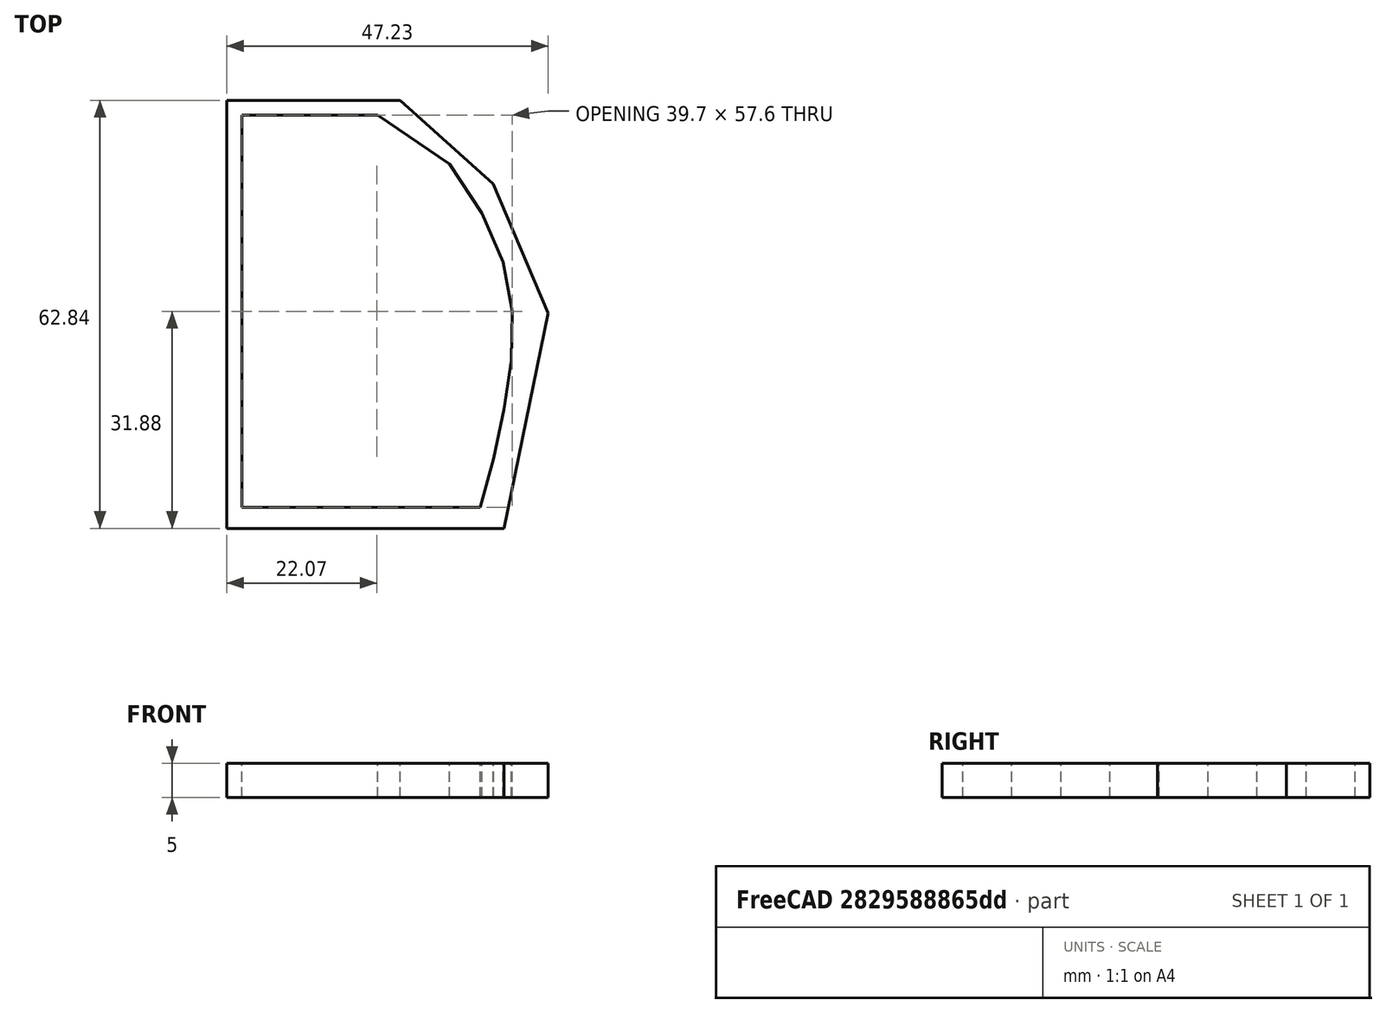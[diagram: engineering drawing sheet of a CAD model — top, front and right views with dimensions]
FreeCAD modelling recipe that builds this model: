
FCSTD DOCUMENT  (FreeCAD 0.19R24291 (Git))
Label: test-profile-plate
License: All rights reserved
LicenseURL: http://en.wikipedia.org/wiki/All_rights_reserved
objects: Sketcher::SketchObject×1, PartDesign::Pad×1, PartDesign::Body×1
note: 4 computed .brp shape members not serialized (recipe doc carries the construction recipe); baked Part::Feature solids carry a one-line shape summary decoded from their .brp

FEATURE [Sketcher::SketchObject] Sketch
  FullyConstrained = false
  MapMode = 5
  Support = -> [XY_Plane]
  sketch-geometry (6):
    g0: LineSegment StartX=-2.21516 StartY=59.7598 StartZ=0 EndX=-2.21516 EndY=-3.07541 EndZ=0
    g1: LineSegment StartX=-2.21516 StartY=-3.07541 StartZ=0 EndX=38.4894 EndY=-3.07541 EndZ=0
    g2: LineSegment StartX=38.4894 StartY=-3.07541 StartZ=0 EndX=45.01 EndY=28.5398 EndZ=0
    g3: LineSegment StartX=45.01 StartY=28.5398 StartZ=0 EndX=36.9087 EndY=47.5089 EndZ=0
    g4: LineSegment StartX=36.9087 StartY=47.5089 StartZ=0 EndX=23.2746 EndY=59.7598 EndZ=0
    g5: LineSegment StartX=23.2746 StartY=59.7598 StartZ=0 EndX=-2.21516 EndY=59.7598 EndZ=0
  constraints (9):
    c: Vertical(g0)
    c: Coincident(g0,g1)
    c: Horizontal(g1)
    c: Coincident(g1,g2)
    c: Coincident(g2,g3)
    c: Coincident(g3,g4)
    c: Coincident(g4,g5)
    c: Coincident(g5,g0)
    c: Horizontal(g5)
FEATURE [PartDesign::Pad] Pad
  Direction = (1,1,1)
  Length = 5
  Length2 = 100
  Profile = -> Sketch
  Type = 0
FEATURE [PartDesign::Body] Body
  Group = -> [Sketch,Pad]
  Origin = -> Origin
  Tip = -> Pad
